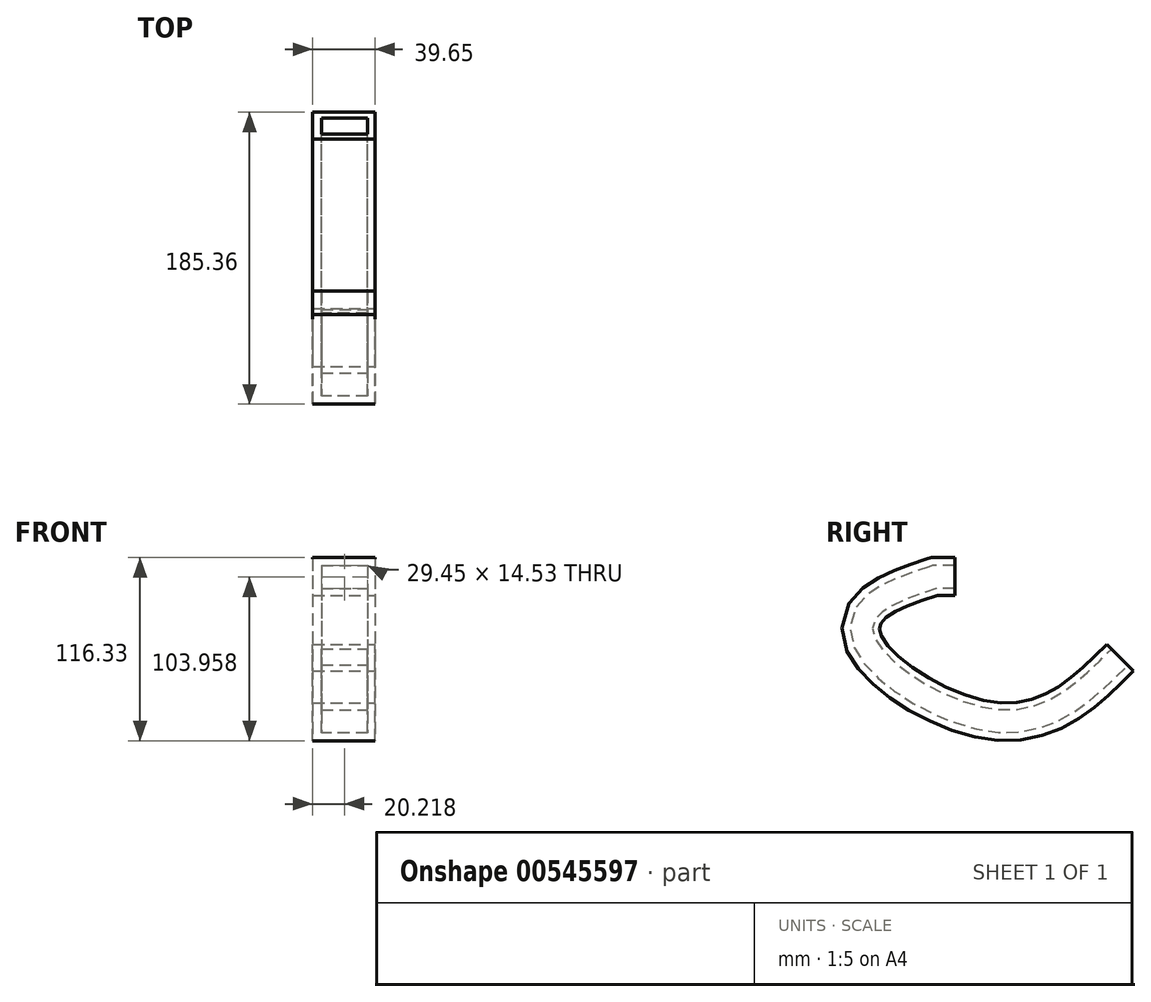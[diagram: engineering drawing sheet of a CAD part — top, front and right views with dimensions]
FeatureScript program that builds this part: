
annotation { "Feature Type Name" : "Feature", "Feature Type Description" : "" }
export const myFeature = defineFeature(function(context is Context, id is Id, definition is map)
    precondition{}
    {
        {
            var Q0;
            Q0=qCreatedBy(makeId("Front.planeOp"),FACE);
            var sketch = newSketch(context, id + "F0", { "sketchPlane" : qUnion([Q0])});
            skLineSegment(sketch, "E0.bottom", {"start": v(-60.96, 55.07) * mm, "end": v(-21.3, 55.07) * mm});
            skLineSegment(sketch, "E0.top", {"start": v(-60.96, 31.11) * mm, "end": v(-21.3, 31.11) * mm});
            skLineSegment(sketch, "E0.left", {"start": v(-60.96, 55.07) * mm, "end": v(-60.96, 31.11) * mm});
            skLineSegment(sketch, "E0.right", {"start": v(-21.3, 55.07) * mm, "end": v(-21.3, 31.11) * mm});
            skLineSegment(sketch, "E1.bottom", {"start": v(-55.47, 49.96) * mm, "end": v(-26.02, 49.96) * mm});
            skLineSegment(sketch, "E1.top", {"start": v(-55.47, 35.43) * mm, "end": v(-26.02, 35.43) * mm});
            skLineSegment(sketch, "E1.left", {"start": v(-55.47, 49.96) * mm, "end": v(-55.47, 35.43) * mm});
            skLineSegment(sketch, "E1.right", {"start": v(-26.02, 49.96) * mm, "end": v(-26.02, 35.43) * mm});
            skSolve(sketch);
        }
        {
            var Q0;
            Q0=qCreatedBy(makeId("Right.planeOp"),FACE);
            var sketch = newSketch(context, id + "F1", { "sketchPlane" : qUnion([Q0])});
            skLineSegment(sketch, "E2", {"start": v(0, 35.43) * mm, "end": v(-11.7, 35.43) * mm});
            skFitSpline(sketch, "E3", {"points": [v(-11.7, 35.43) * mm, v(-52.08, 8.7) * mm, v(28.11, -41.42) * mm, v(99.68, -3) * mm], "startDerivative": vector(-231, -76.93) * mm, "endDerivative": vector(174.61, 175.08) * mm});
            skSolve(sketch);
        }
        {
            var Q0;
            Q0 = qSketchRegion(id + "F0", true);
            var Q1;
            Q1 = qConstructionFilter(qBodyType(qCreatedBy(id + "F1" ,EDGE), BodyType.WIRE), ConstructionObject.NO);
            sweep(context, id + "F2", {"profiles" : qUnion([Q0]), "path" : qUnion([Q1])});
        }
    });
